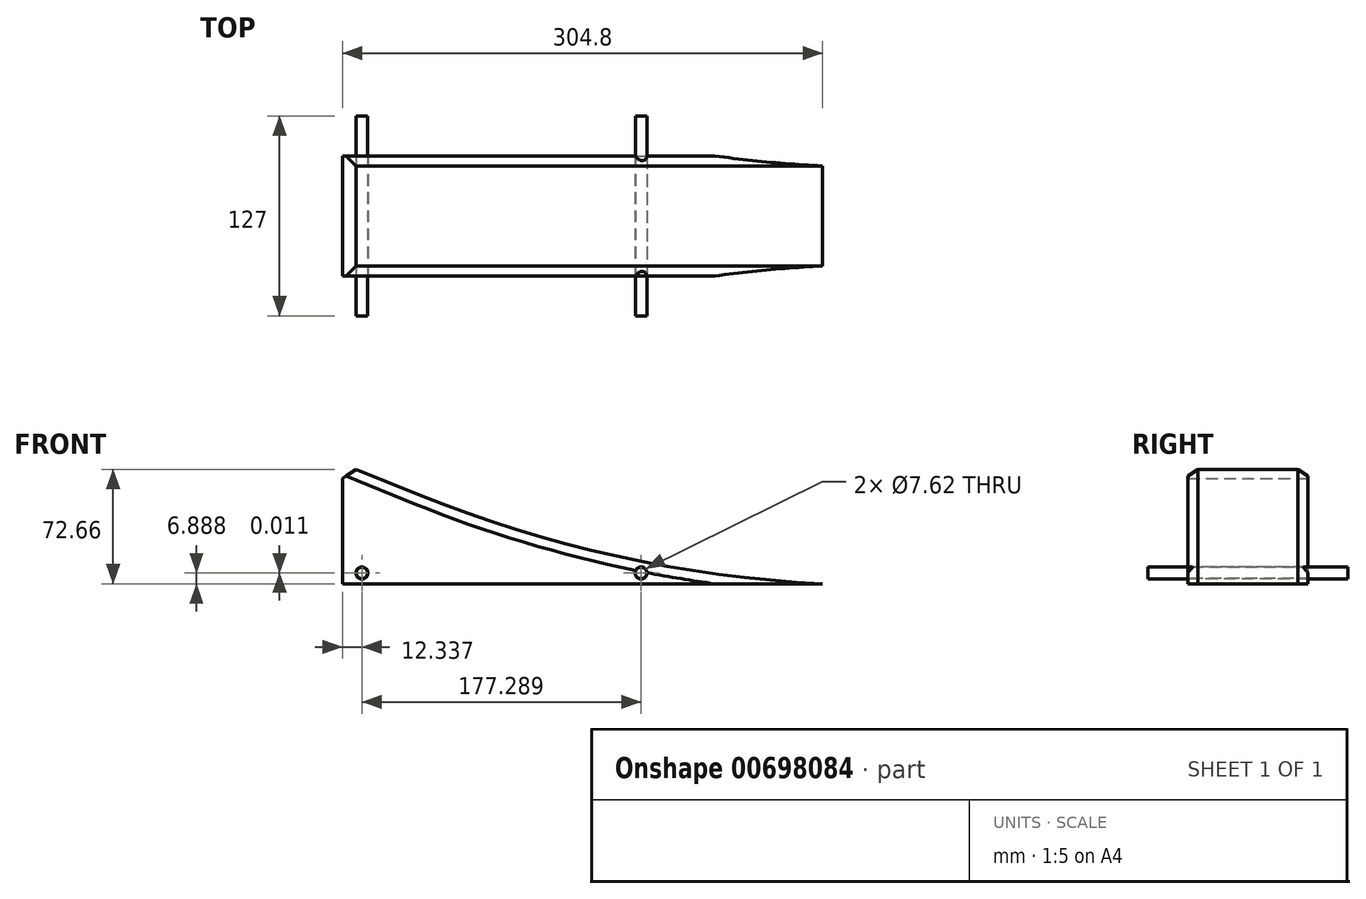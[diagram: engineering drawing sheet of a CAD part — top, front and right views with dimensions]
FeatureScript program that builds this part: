
annotation { "Feature Type Name" : "Feature", "Feature Type Description" : "" }
export const myFeature = defineFeature(function(context is Context, id is Id, definition is map)
    precondition{}
    {
        {
            var Q0;
            Q0=qCreatedBy(makeId("Front.planeOp"),FACE);
            var sketch = newSketch(context, id + "F0", { "sketchPlane" : qUnion([Q0])});
            skLineSegment(sketch, "E0", {"start": v(-12.48, 0) * mm, "end": v(-317.28, 0) * mm});
            skLineSegment(sketch, "E1", {"start": v(-317.28, 0) * mm, "end": v(-317.28, 76.2) * mm});
            skLineSegment(sketch, "E2", {"start": v(-317.28, 76.2) * mm, "end": v(-269.18, 56.72) * mm});
            skArc(sketch, "E3", {"start": v(-269.18, 56.72) * mm, "mid": v(-143.2, 17.6) * mm, "end": v(-12.48, 0) * mm});
            skSolve(sketch);
        }
        {
            var Q0;
            Q0=makeQuery(id+"F0.imprint","IMPRINT",FACE,{"disambiguationData":[TD([[makeQuery(id+"F0.imprint","IMPRINT",EDGE,{"derivedFrom":sQuery(id+"F0.wireOp",EDGE,"E0")}),-1.0]])]});
            extrude(context, id + "F1", {"entities" : qUnion([Q0]), "depth" : 76.2 * mm, "offsetDistance" : 25.4 * mm});
        }
        {
            var Q0;
            Q0=makeQuery(id+"F1.opExtrude","CAP_FACE",FACE,{"disambiguationData":[OSD([sQuery(id+"F0.wireOp",EDGE,"E0"),sQuery(id+"F0.wireOp",EDGE,"E1"),sQuery(id+"F0.wireOp",EDGE,"E2"),sQuery(id+"F0.wireOp",EDGE,"E3")])],"isStart":false});
            var sketch = newSketch(context, id + "F2", { "sketchPlane" : qUnion([Q0])});
            skCircle(sketch, "E4", {"center": v(-304.94, 6.89) * mm, "radius": 3.8 * mm});
            skCircle(sketch, "E5", {"center": v(-127.65, 6.9) * mm, "radius": 3.81 * mm});
            skSolve(sketch);
        }
        {
            var Q0;
            Q0=makeQuery(id+"F2.imprint","IMPRINT",FACE,{"disambiguationData":[TD([[makeQuery(id+"F2.imprint","IMPRINT",EDGE,{"derivedFrom":sQuery(id+"F2.wireOp",EDGE,"E4")}),1.0]])]});
            var Q1;
            Q1=makeQuery(id+"F2.imprint","IMPRINT",FACE,{"disambiguationData":[TD([[makeQuery(id+"F2.imprint","IMPRINT",EDGE,{"derivedFrom":sQuery(id+"F2.wireOp",EDGE,"E5")}),1.0]])]});
            extrude(context, id + "F3", {"entities" : qUnion([Q0, Q1]), "operationType" : NewBodyOperationType.REMOVE, "oppositeDirection" : true, "depth" : 76.2 * mm, "offsetDistance" : 25.4 * mm});
        }
        {
            var Q0;
            Q0=makeQuery(id+"F1.opExtrude","CAP_EDGE",EDGE,{"disambiguationData":[OSD([sQuery(id+"F0.wireOp",EDGE,"E2")])],"isStart":true});
            var Q1;
            Q1=makeQuery(id+"F1.opExtrude","CAP_EDGE",EDGE,{"disambiguationData":[OSD([sQuery(id+"F0.wireOp",EDGE,"E3")])],"isStart":false});
            var Q2;
            Q2=makeQuery(id+"F1.opExtrude","SWEPT_EDGE",EDGE,{"disambiguationData":[OSD([sQuery(id+"F0.wireOp",EDGE,"E1"),sQuery(id+"F0.wireOp",EDGE,"E2")])]});
            chamfer(context, id + "F4", {"entities" : qUnion([Q0, Q1, Q2]), "width" : 6.35 * mm, "tangentPropagation" : true});
        }
        {
            var Q0;
            Q0=makeQuery(id+"F1.opExtrude","CAP_FACE",FACE,{"disambiguationData":[OSD([sQuery(id+"F0.wireOp",EDGE,"E0"),sQuery(id+"F0.wireOp",EDGE,"E1"),sQuery(id+"F0.wireOp",EDGE,"E2"),sQuery(id+"F0.wireOp",EDGE,"E3")])],"isStart":false});
            var sketch = newSketch(context, id + "F5", { "sketchPlane" : qUnion([Q0])});
            skCircle(sketch, "E6", {"center": v(-304.94, 6.89) * mm, "radius": 3.57 * mm});
            skCircle(sketch, "E7", {"center": v(-127.65, 6.9) * mm, "radius": 3.68 * mm});
            skSolve(sketch);
        }
        {
            var Q0;
            Q0=makeQuery(id+"F5.imprint","IMPRINT",FACE,{"disambiguationData":[TD([[makeQuery(id+"F5.imprint","IMPRINT",EDGE,{"derivedFrom":sQuery(id+"F5.wireOp",EDGE,"E6")}),1.0]])]});
            extrude(context, id + "F6", {"entities" : qUnion([Q0]), "oppositeDirection" : true, "depth" : 101.6 * mm, "offsetDistance" : 25.4 * mm});
        }
        {
            var Q0;
            Q0 = qSketchRegion(id + "F5", true);
            var Q1;
            Q1=makeQuery(id+"F6.opExtrude","CAP_FACE",FACE,{"disambiguationData":[OSD([sQuery(id+"F5.wireOp",EDGE,"E6")])],"isStart":true});
            extrude(context, id + "F7", {"entities" : qUnion([Q0, Q1]), "operationType" : NewBodyOperationType.ADD, "depth" : 25.4 * mm, "offsetDistance" : 25.4 * mm});
        }
        {
            var Q0;
            Q0 = qSketchRegion(id + "F5", true);
            extrude(context, id + "F8", {"entities" : qUnion([Q0]), "oppositeDirection" : true, "depth" : 101.6 * mm, "offsetDistance" : 25.4 * mm});
        }
    });
